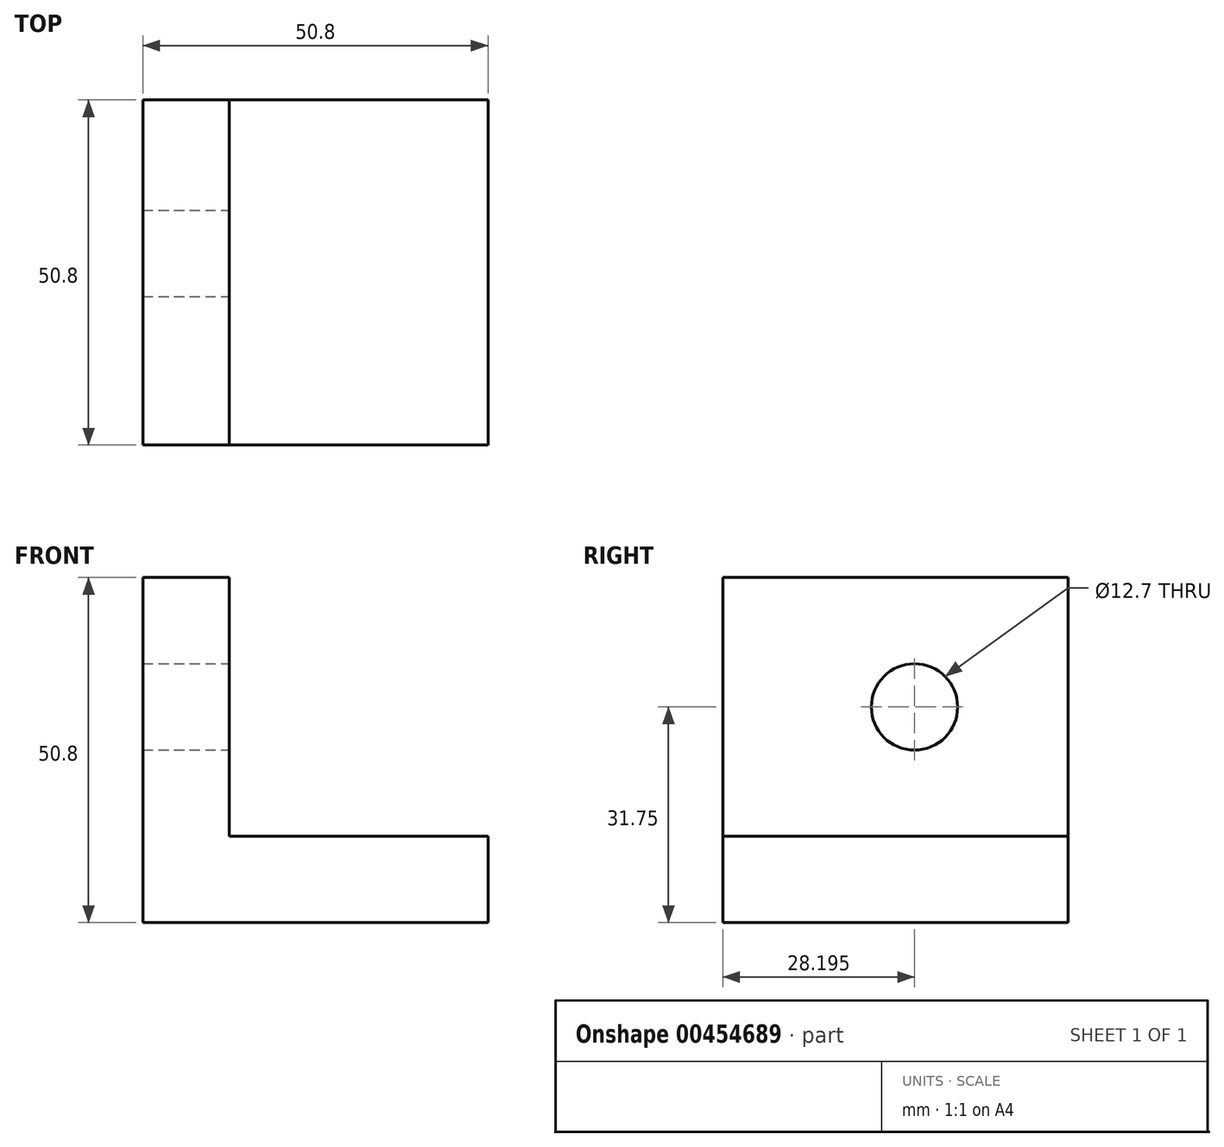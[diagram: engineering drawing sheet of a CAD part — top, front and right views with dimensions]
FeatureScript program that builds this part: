
annotation { "Feature Type Name" : "Feature", "Feature Type Description" : "" }
export const myFeature = defineFeature(function(context is Context, id is Id, definition is map)
    precondition{}
    {
        {
            var Q0;
            Q0=qCreatedBy(makeId("Top.planeOp"),FACE);
            var sketch = newSketch(context, id + "F0", { "sketchPlane" : qUnion([Q0])});
            skLineSegment(sketch, "E0.bottom", {"start": v(-24.99, 19.18) * mm, "end": v(25.81, 19.18) * mm});
            skLineSegment(sketch, "E0.top", {"start": v(-24.99, -31.62) * mm, "end": v(25.81, -31.62) * mm});
            skLineSegment(sketch, "E0.left", {"start": v(-24.99, 19.18) * mm, "end": v(-24.99, -31.62) * mm});
            skLineSegment(sketch, "E0.right", {"start": v(25.81, 19.18) * mm, "end": v(25.81, -31.62) * mm});
            skSolve(sketch);
        }
        {
            var Q0;
            Q0=makeQuery(id+"F0.imprint","IMPRINT",FACE,{"disambiguationData":[TD([[makeQuery(id+"F0.imprint","IMPRINT",EDGE,{"derivedFrom":sQuery(id+"F0.wireOp",EDGE,"E0.bottom")}),-1.0]])]});
            extrude(context, id + "F1", {"entities" : qUnion([Q0]), "depth" : 12.7 * mm});
        }
        {
            var Q0;
            Q0=makeQuery(id+"F1.opExtrude","CAP_FACE",FACE,{"disambiguationData":[OSD([sQuery(id+"F0.wireOp",EDGE,"E0.bottom"),sQuery(id+"F0.wireOp",EDGE,"E0.top"),sQuery(id+"F0.wireOp",EDGE,"E0.left"),sQuery(id+"F0.wireOp",EDGE,"E0.right")])],"isStart":false});
            var sketch = newSketch(context, id + "F2", { "sketchPlane" : qUnion([Q0])});
            skLineSegment(sketch, "E1.bottom", {"start": v(-24.99, 19.18) * mm, "end": v(-12.29, 19.18) * mm});
            skLineSegment(sketch, "E1.top", {"start": v(-24.99, -31.62) * mm, "end": v(-12.29, -31.62) * mm});
            skLineSegment(sketch, "E1.left", {"start": v(-24.99, 19.18) * mm, "end": v(-24.99, -31.62) * mm});
            skLineSegment(sketch, "E1.right", {"start": v(-12.29, 19.18) * mm, "end": v(-12.29, -31.62) * mm});
            skSolve(sketch);
        }
        {
            var Q0;
            Q0=makeQuery(id+"F2.imprint","IMPRINT",FACE,{"disambiguationData":[TD([[makeQuery(id+"F2.imprint","IMPRINT",EDGE,{"derivedFrom":sQuery(id+"F2.wireOp",EDGE,"E1.bottom")}),-1.0]])]});
            extrude(context, id + "F3", {"entities" : qUnion([Q0]), "operationType" : NewBodyOperationType.ADD, "depth" : 38.1 * mm});
        }
        {
            var Q0;
            Q0=makeQuery(id+"F3.opExtrude","SWEPT_FACE",FACE,{"disambiguationData":[OSD([sQuery(id+"F2.wireOp",EDGE,"E1.right")])]});
            var sketch = newSketch(context, id + "F4", { "sketchPlane" : qUnion([Q0])});
            skCircle(sketch, "E2", {"center": v(-3.43, 31.75) * mm, "radius": 6.35 * mm});
            skPoint(sketch, "E2.centerSnap0", {"position": v(-31.62, 31.75) * mm});
            skSolve(sketch);
        }
        {
            var Q0;
            Q0=makeQuery(id+"F4.imprint","IMPRINT",FACE,{"disambiguationData":[TD([[makeQuery(id+"F4.imprint","IMPRINT",EDGE,{"derivedFrom":sQuery(id+"F4.wireOp",EDGE,"E2")}),1.0]])]});
            extrude(context, id + "F5", {"entities" : qUnion([Q0]), "operationType" : NewBodyOperationType.REMOVE, "oppositeDirection" : true, "depth" : 25.4 * mm});
        }
    });
